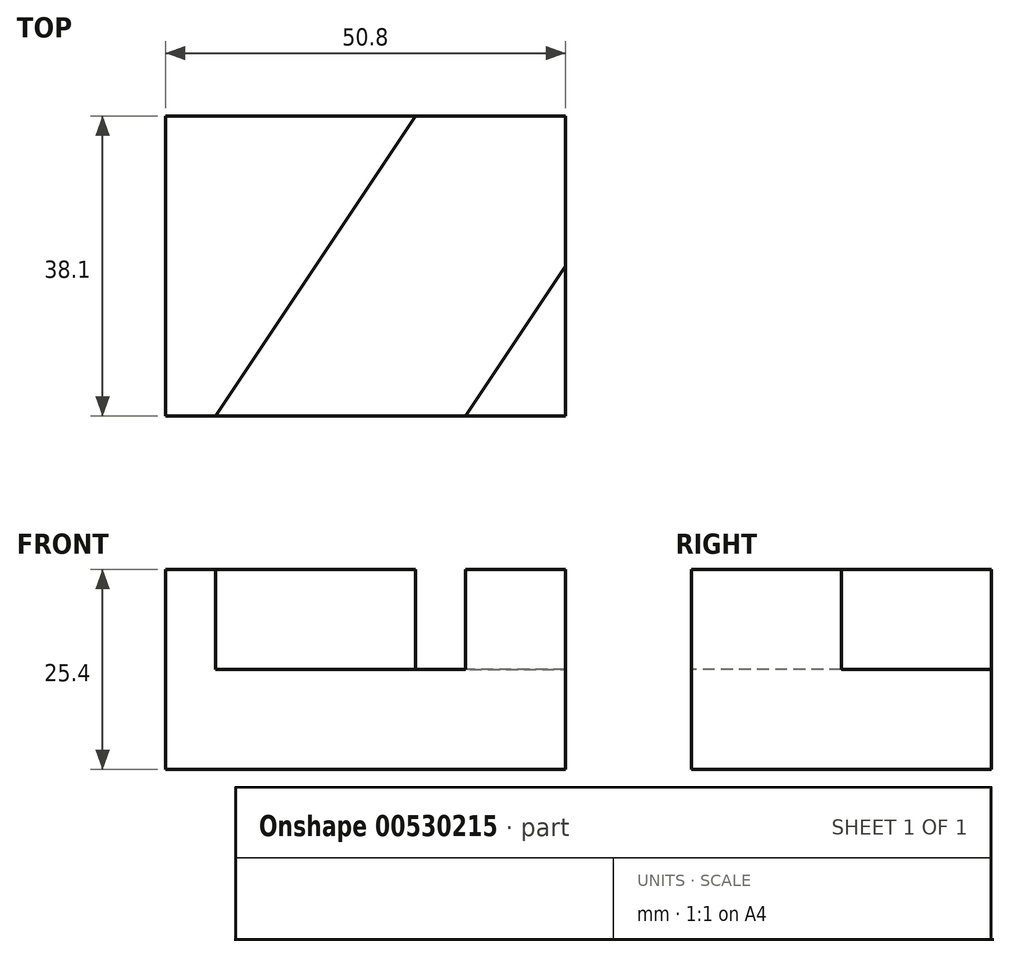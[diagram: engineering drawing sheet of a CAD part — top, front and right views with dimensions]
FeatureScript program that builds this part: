
annotation { "Feature Type Name" : "Feature", "Feature Type Description" : "" }
export const myFeature = defineFeature(function(context is Context, id is Id, definition is map)
    precondition{}
    {
        {
            var Q0;
            Q0=qCreatedBy(makeId("Front.planeOp"),FACE);
            var sketch = newSketch(context, id + "F0", { "sketchPlane" : qUnion([Q0])});
            skLineSegment(sketch, "E0", {"start": v(0, 0) * mm, "end": v(-50.8, 0) * mm});
            skLineSegment(sketch, "E1", {"start": v(-50.8, 0) * mm, "end": v(-50.8, 12.7) * mm});
            skLineSegment(sketch, "E2", {"start": v(-50.8, 12.7) * mm, "end": v(0, 12.7) * mm});
            skLineSegment(sketch, "E3", {"start": v(0, 12.7) * mm, "end": v(0, 0) * mm});
            skSolve(sketch);
        }
        {
            var Q0;
            Q0=makeQuery(id+"F0.imprint","IMPRINT",FACE,{"disambiguationData":[TD([[makeQuery(id+"F0.imprint","IMPRINT",EDGE,{"derivedFrom":sQuery(id+"F0.wireOp",EDGE,"E0")}),-1.0]])]});
            extrude(context, id + "F1", {"entities" : qUnion([Q0]), "depth" : 38.1 * mm, "offsetDistance" : 25.4 * mm});
        }
        {
            var Q0;
            Q0=makeQuery(id+"F1.opExtrude","SWEPT_FACE",FACE,{"disambiguationData":[OSD([sQuery(id+"F0.wireOp",EDGE,"E2")])]});
            var sketch = newSketch(context, id + "F2", { "sketchPlane" : qUnion([Q0])});
            skLineSegment(sketch, "E4", {"start": v(-19.05, 0) * mm, "end": v(-44.45, -38.1) * mm});
            skSolve(sketch);
        }
        {
            var Q0;
            {var subQ0=sQuery(id+"F2.wireOp",EDGE,"E4");Q0=makeQuery(id+"F2.imprint","IMPRINT",FACE,{"disambiguationData":[TD([[makeQuery(id+"F2.imprint","IMPRINT",EDGE,{"derivedFrom":subQ0}),-1.0]])]});}
            extrude(context, id + "F3", {"entities" : qUnion([Q0]), "operationType" : NewBodyOperationType.ADD, "depth" : 12.7 * mm, "offsetDistance" : 25.4 * mm});
        }
        {
            var Q0;
            Q0=makeQuery(id+"F1.opExtrude","SWEPT_FACE",FACE,{"disambiguationData":[OSD([sQuery(id+"F0.wireOp",EDGE,"E2")])]});
            var sketch = newSketch(context, id + "F4", { "sketchPlane" : qUnion([Q0])});
            skLineSegment(sketch, "E5", {"start": v(0, -19.05) * mm, "end": v(-12.7, -38.1) * mm});
            skSolve(sketch);
        }
        {
            var Q0;
            {var subQ0=sQuery(id+"F4.wireOp",EDGE,"E5");Q0=makeQuery(id+"F4.imprint","IMPRINT",FACE,{"disambiguationData":[TD([[makeQuery(id+"F4.imprint","IMPRINT",EDGE,{"derivedFrom":subQ0}),1.0]])]});}
            extrude(context, id + "F5", {"entities" : qUnion([Q0]), "operationType" : NewBodyOperationType.ADD, "depth" : 12.7 * mm, "offsetDistance" : 25.4 * mm});
        }
    });
